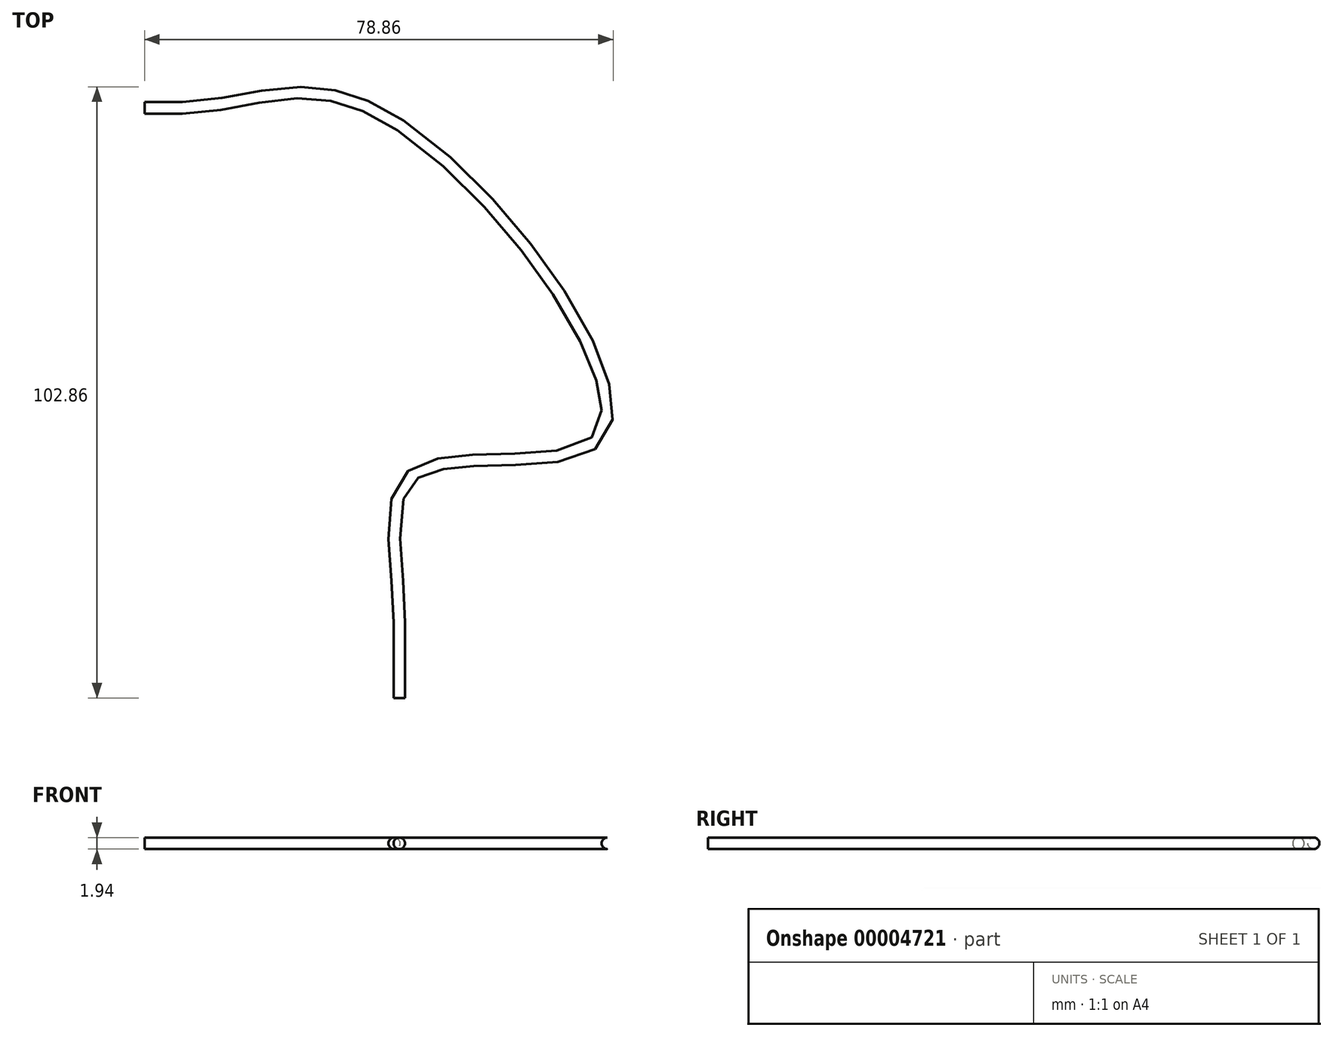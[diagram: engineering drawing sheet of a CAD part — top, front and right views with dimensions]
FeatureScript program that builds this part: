
annotation { "Feature Type Name" : "Feature", "Feature Type Description" : "" }
export const myFeature = defineFeature(function(context is Context, id is Id, definition is map)
    precondition{}
    {
        {
            var Q0;
            Q0=qCreatedBy(makeId("Top.planeOp"),FACE);
            var sketch = newSketch(context, id + "F0", { "sketchPlane" : qUnion([Q0])});
            skLineSegment(sketch, "E0", {"start": v(0, 0) * mm, "end": v(0, 12.7) * mm});
            skFitSpline(sketch, "E1", {"points": [v(0, 12.7) * mm, v(3.16, 38.18) * mm, v(34.09, 44.43) * mm, v(-4, 98.87) * mm, v(-36.53, 99.34) * mm], "startDerivative": vector(0, 160.54) * mm, "endDerivative": vector(-133.98, 0) * mm});
            skLineSegment(sketch, "E2", {"start": v(-36.53, 99.34) * mm, "end": v(-42.88, 99.34) * mm});
            skSolve(sketch);
        }
        {
            var Q0;
            Q0=qCreatedBy(makeId("Front.planeOp"),FACE);
            var sketch = newSketch(context, id + "F1", { "sketchPlane" : qUnion([Q0])});
            skCircle(sketch, "E3", {"center": v(0, 0) * mm, "radius": 0.97 * mm});
            skSolve(sketch);
        }
        {
            var Q0;
            Q0 = qSketchRegion(id + "F1", true);
            var Q1;
            Q1=sQuery(id+"F0.wireOp",EDGE,"E0");
            var Q2;
            Q2=sQuery(id+"F0.wireOp",EDGE,"E1");
            var Q3;
            Q3=sQuery(id+"F0.wireOp",EDGE,"E2");
            sweep(context, id + "F2", {"profiles" : qUnion([Q0]), "path" : qUnion([Q1, Q2, Q3])});
        }
    });
